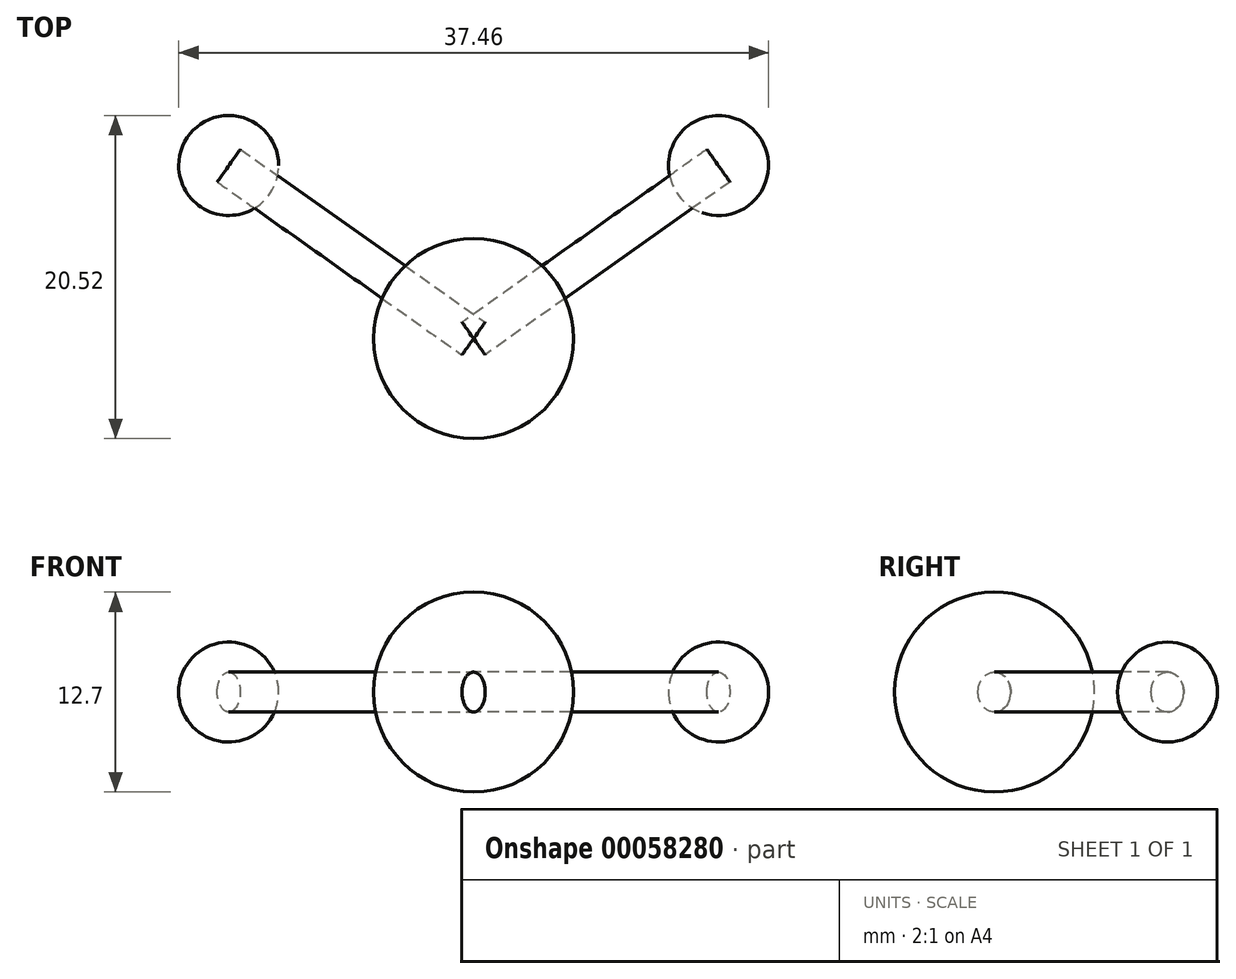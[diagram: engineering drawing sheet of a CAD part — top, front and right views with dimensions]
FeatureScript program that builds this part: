
annotation { "Feature Type Name" : "Feature", "Feature Type Description" : "" }
export const myFeature = defineFeature(function(context is Context, id is Id, definition is map)
    precondition{}
    {
        {
            var Q0;
            Q0=qCreatedBy(makeId("Top.planeOp"),FACE);
            var sketch = newSketch(context, id + "F0", { "sketchPlane" : qUnion([Q0])});
            skCircle(sketch, "E0", {"center": v(0, 0) * mm, "radius": 6.35 * mm, "construction": true});
            skCircle(sketch, "E1", {"center": v(15.56, 11) * mm, "radius": 3.18 * mm, "construction": true});
            skCircle(sketch, "E2", {"center": v(-15.56, 11) * mm, "radius": 3.18 * mm, "construction": true});
            skLineSegment(sketch, "E3", {"start": v(0, 0) * mm, "end": v(-15.56, 11) * mm, "construction": true});
            skLineSegment(sketch, "E4", {"start": v(0, 0) * mm, "end": v(15.56, 11) * mm, "construction": true});
            skLineSegment(sketch, "E5", {"start": v(-15.56, 11) * mm, "end": v(15.56, 11) * mm, "construction": true});
            skSolve(sketch);
        }
        {
            var Q0;
            Q0=qCreatedBy(makeId("Top.planeOp"),FACE);
            var sketch = newSketch(context, id + "F1", { "sketchPlane" : qUnion([Q0])});
            skArc(sketch, "E6", {"start": v(-6.35, 0) * mm, "mid": v(0, -6.35) * mm, "end": v(6.35, 0) * mm});
            skLineSegment(sketch, "E7", {"start": v(-6.35, 0) * mm, "end": v(6.35, 0) * mm});
            skSolve(sketch);
        }
        {
            var Q0;
            Q0=makeQuery(id+"F1.imprint","IMPRINT",FACE,{"disambiguationData":[TD([[makeQuery(id+"F1.imprint","IMPRINT",EDGE,{"derivedFrom":sQuery(id+"F1.wireOp",EDGE,"E6")}),1.0]])]});
            var Q1;
            Q1=sQuery(id+"F1.wireOp",EDGE,"E7");
            revolve(context, id + "F2", {"entities" : qUnion([Q0]), "axis" : qUnion([Q1]), "revolveType" : RevolveType.FULL});
        }
        {
            var Q0;
            Q0=qCreatedBy(makeId("Top.planeOp"),FACE);
            var sketch = newSketch(context, id + "F3", { "sketchPlane" : qUnion([Q0])});
            skArc(sketch, "E8", {"start": v(-18.73, 11) * mm, "mid": v(-15.56, 7.82) * mm, "end": v(-12.38, 11) * mm});
            skLineSegment(sketch, "E9", {"start": v(-18.73, 11) * mm, "end": v(-12.38, 11) * mm});
            skSolve(sketch);
        }
        {
            var Q0;
            Q0=makeQuery(id+"F3.imprint","IMPRINT",FACE,{"disambiguationData":[TD([[makeQuery(id+"F3.imprint","IMPRINT",EDGE,{"derivedFrom":sQuery(id+"F3.wireOp",EDGE,"E8")}),1.0]])]});
            var Q1;
            Q1=sQuery(id+"F3.wireOp",EDGE,"E9");
            revolve(context, id + "F4", {"entities" : qUnion([Q0]), "axis" : qUnion([Q1]), "revolveType" : RevolveType.FULL});
        }
        {
            var Q0;
            Q0=qCreatedBy(makeId("Front.planeOp"),FACE);
            var sketch = newSketch(context, id + "F5", { "sketchPlane" : qUnion([Q0])});
            skLineSegment(sketch, "E10", {"start": v(0, -2.93) * mm, "end": v(0, 22.47) * mm, "construction": true});
            skSolve(sketch);
        }
        {
            var Q0;
            Q0=makeQuery(id+"F4.opRevolve","SWEPT_BODY",BODY,{"disambiguationData":[OSD([sQuery(id+"F3.wireOp",EDGE,"E8"),sQuery(id+"F3.wireOp",EDGE,"E9")])]});
            var Q1;
            Q1=sQuery(id+"F5.wireOp",EDGE,"E10");
            circularPattern(context, id + "F6", {"entities" : qUnion([Q0]), "axis" : qUnion([Q1]), "angle" : 109.5 * degree, "instanceCount" : 2, "oppositeDirection" : true});
        }
        {
            var Q0;
            Q0=sQuery(id+"F5.wireOp",EDGE,"E10");
            cPlane(context, id + "F7", {"entities" : qUnion([Q0]), "cplaneType" : CPlaneType.LINE_ANGLE, "offset" : 152.4 * mm, "angle" : 35.25 * degree, "width" : 152.4 * mm, "height" : 152.4 * mm});
        }
        {
            var Q0;
            Q0=qCreatedBy(id+"F7.planeOp",FACE);
            var sketch = newSketch(context, id + "F8", { "sketchPlane" : qUnion([Q0])});
            skCircle(sketch, "E11", {"center": v(0, 0) * mm, "radius": 1.27 * mm});
            skSolve(sketch);
        }
        {
            var Q0;
            Q0 = qSketchRegion(id + "F8", true);
            extrude(context, id + "F9", {"entities" : qUnion([Q0]), "depth" : 19.04 * mm});
        }
        {
            var Q0;
            Q0=makeQuery(id+"F9.opExtrude","SWEPT_BODY",BODY,{"disambiguationData":[OSD([sQuery(id+"F8.wireOp",EDGE,"E11")])]});
            var Q1;
            Q1=sQuery(id+"F5.wireOp",EDGE,"E10");
            circularPattern(context, id + "F10", {"entities" : qUnion([Q0]), "axis" : qUnion([Q1]), "angle" : 109.5 * degree, "instanceCount" : 2});
        }
    });
